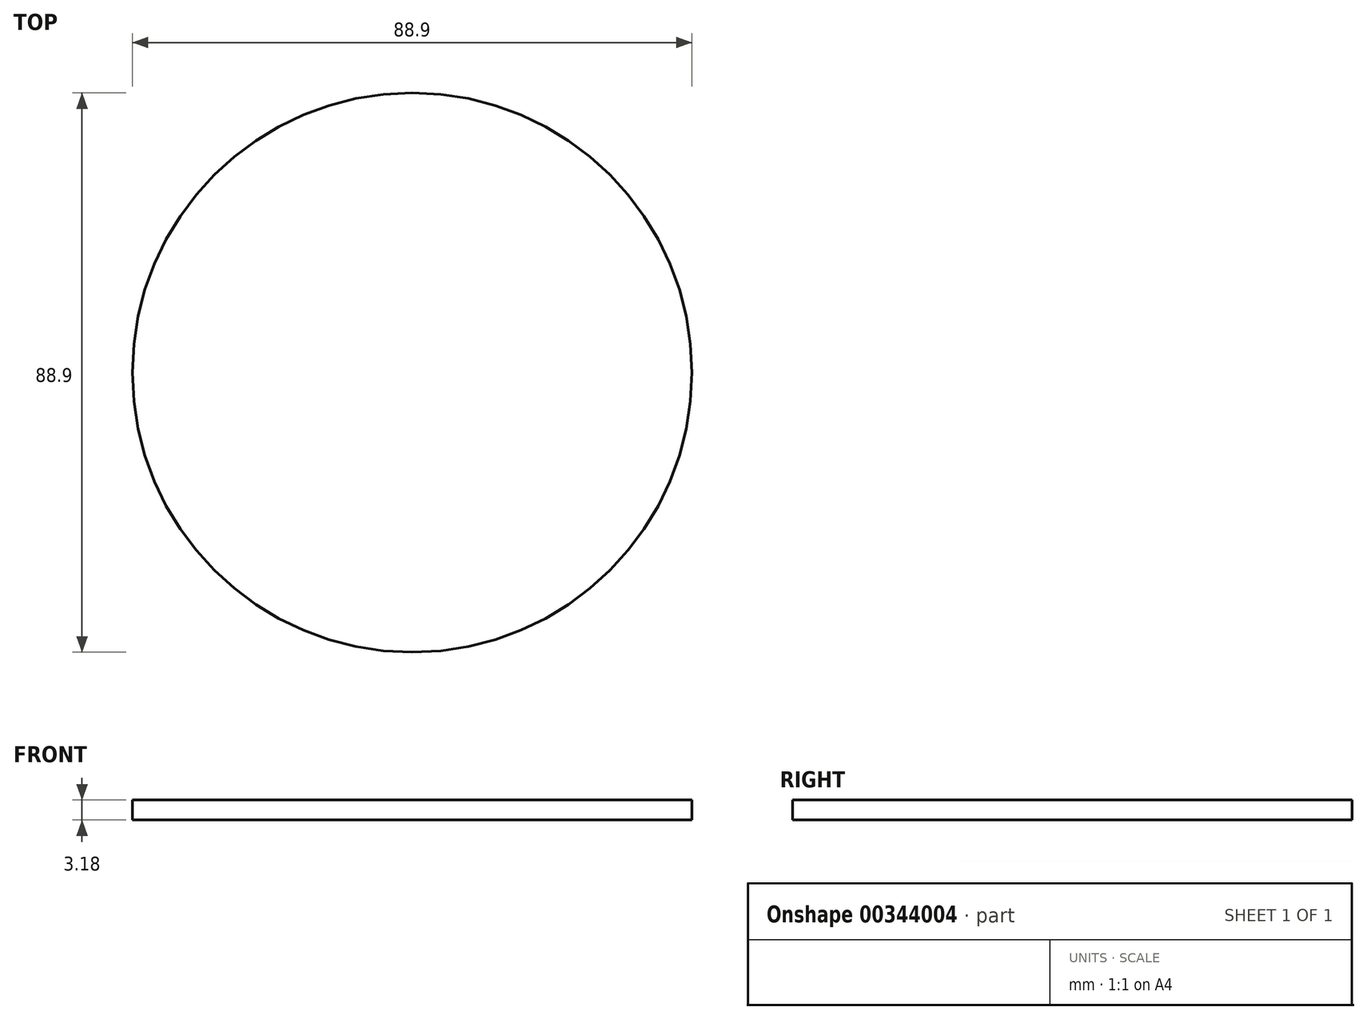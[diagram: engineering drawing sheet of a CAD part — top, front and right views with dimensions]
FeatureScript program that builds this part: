
annotation { "Feature Type Name" : "Feature", "Feature Type Description" : "" }
export const myFeature = defineFeature(function(context is Context, id is Id, definition is map)
    precondition{}
    {
        {
            var Q0;
            Q0=qCreatedBy(makeId("Top.planeOp"),FACE);
            var sketch = newSketch(context, id + "F0", { "sketchPlane" : qUnion([Q0])});
            skCircle(sketch, "E0", {"center": v(0, 0) * mm, "radius": 14.85 * mm});
            skCircle(sketch, "E1", {"center": v(0, 0) * mm, "radius": 20.25 * mm});
            skCircle(sketch, "E2", {"center": v(0, 0) * mm, "radius": 44.45 * mm});
            skSolve(sketch);
        }
        {
            var Q0;
            Q0 = qSketchRegion(id + "F0", true);
            var Q1;
            Q1=makeQuery(id+"F0.imprint","IMPRINT",FACE,{"disambiguationData":[TD([[makeQuery(id+"F0.imprint","IMPRINT",EDGE,{"derivedFrom":sQuery(id+"F0.wireOp",EDGE,"E0")}),1.0]])]});
            var Q2;
            Q2=makeQuery(id+"F0.imprint","IMPRINT",FACE,{"disambiguationData":[TD([[makeQuery(id+"F0.imprint","IMPRINT",EDGE,{"derivedFrom":sQuery(id+"F0.wireOp",EDGE,"E0")}),-1.0]])]});
            extrude(context, id + "F1", {"entities" : qUnion([Q0, Q1, Q2]), "oppositeDirection" : true, "depth" : 3.17 * mm, "hasSecondDirection" : true, "secondDirectionOppositeDirection" : false, "secondDirectionDepth" : 0 * mm});
        }
    });
